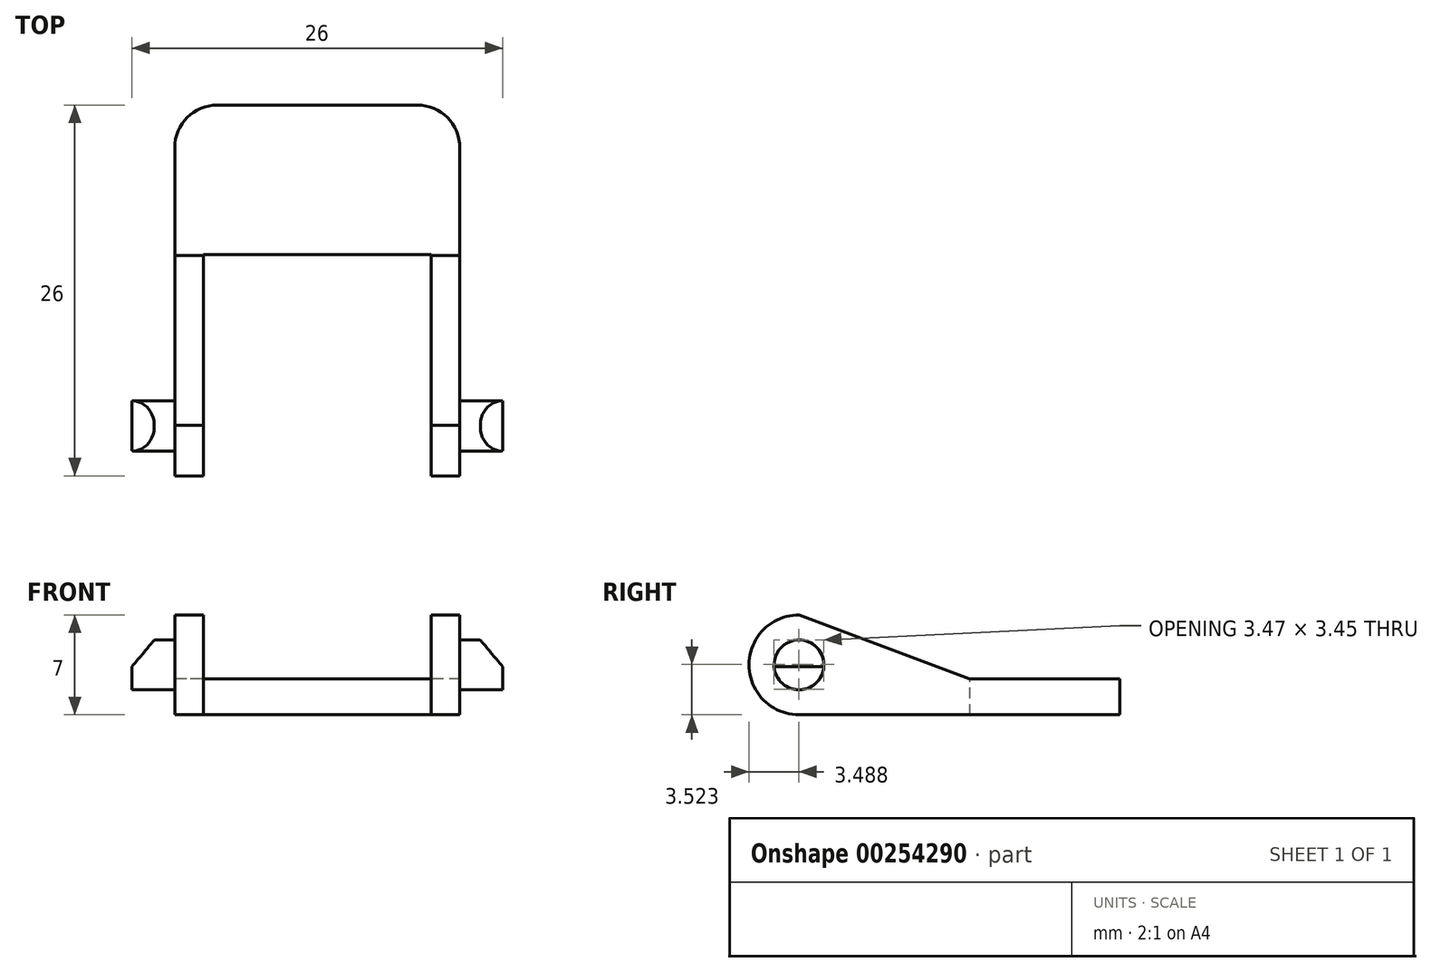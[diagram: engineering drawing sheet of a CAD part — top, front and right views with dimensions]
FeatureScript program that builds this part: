
annotation { "Feature Type Name" : "Feature", "Feature Type Description" : "" }
export const myFeature = defineFeature(function(context is Context, id is Id, definition is map)
    precondition{}
    {
        {
            var Q0;
            Q0=qCreatedBy(makeId("Right.planeOp"),FACE);
            var sketch = newSketch(context, id + "F0", { "sketchPlane" : qUnion([Q0])});
            skLineSegment(sketch, "E0.bottom", {"start": v(-11.1, -3.83) * mm, "end": v(14.9, -3.83) * mm});
            skLineSegment(sketch, "E0.top", {"start": v(-11.1, -6.33) * mm, "end": v(14.9, -6.33) * mm});
            skLineSegment(sketch, "E0.left", {"start": v(-11.1, -3.83) * mm, "end": v(-11.1, -6.33) * mm});
            skLineSegment(sketch, "E0.right", {"start": v(14.9, -3.83) * mm, "end": v(14.9, -6.33) * mm});
            skLineSegment(sketch, "E1", {"start": v(-7.6, -2.83) * mm, "end": v(-7.6, -6.33) * mm});
            skLineSegment(sketch, "E2", {"start": v(-12.06, -7.72) * mm, "end": v(-1, -7.72) * mm});
            skLineSegment(sketch, "E3", {"start": v(-3.27, -2.83) * mm, "end": v(-11.26, -2.83) * mm});
            skPoint(sketch, "E4.orphan", {"position": v(-7.6, -3.83) * mm});
            skCircle(sketch, "E5", {"center": v(-7.6, -2.83) * mm, "radius": 3.5 * mm});
            skLineSegment(sketch, "E6", {"start": v(-7.57, 0.67) * mm, "end": v(4.35, -3.83) * mm});
            skSolve(sketch);
        }
        {
            var Q0;
            {var subQ3=sQuery(id+"F0.wireOp",EDGE,"E3");var subQ7=makeQuery(id+"F0.imprint","INTERSECT",VERTEX,{"derivedFrom":[sQuery(id+"F0.wireOp",EDGE,"E1"),subQ3]});Q0=makeQuery(id+"F0.imprint","IMPRINT",FACE,{"disambiguationData":[TD([[makeQuery(id+"F0.imprint","IMPRINT",EDGE,{"disambiguationData":[TD([[subQ7,-1.0]])],"derivedFrom":subQ3}),-1.0]])]});}
            var Q1;
            {var subQ0=sQuery(id+"F0.wireOp",EDGE,"E5");var subQ1=sQuery(id+"F0.wireOp",EDGE,"E0.bottom");var subQ2=makeQuery(id+"F0.imprint","INTERSECT",VERTEX,{"disambiguationData":[OD(0.0)],"derivedFrom":[subQ1,subQ0]});Q1=makeQuery(id+"F0.imprint","IMPRINT",FACE,{"disambiguationData":[TD([[makeQuery(id+"F0.imprint","IMPRINT",EDGE,{"disambiguationData":[TD([[subQ2,-1.0]])],"derivedFrom":subQ1}),1.0]])]});}
            var Q2;
            {var subQ0=sQuery(id+"F0.wireOp",EDGE,"E1");var subQ1=sQuery(id+"F0.wireOp",EDGE,"E0.bottom");var subQ2=makeQuery(id+"F0.imprint","INTERSECT",VERTEX,{"derivedFrom":[subQ1,subQ0]});Q2=makeQuery(id+"F0.imprint","IMPRINT",FACE,{"disambiguationData":[TD([[makeQuery(id+"F0.imprint","IMPRINT",EDGE,{"disambiguationData":[TD([[subQ2,-1.0]])],"derivedFrom":subQ1}),1.0]])]});}
            var Q3;
            {var subQ0=sQuery(id+"F0.wireOp",EDGE,"E5");var subQ1=sQuery(id+"F0.wireOp",EDGE,"E0.bottom");var subQ2=makeQuery(id+"F0.imprint","INTERSECT",VERTEX,{"disambiguationData":[OD(0.0)],"derivedFrom":[subQ1,subQ0]});Q3=makeQuery(id+"F0.imprint","IMPRINT",FACE,{"disambiguationData":[TD([[makeQuery(id+"F0.imprint","IMPRINT",EDGE,{"disambiguationData":[TD([[subQ2,-1.0]])],"derivedFrom":subQ1}),-1.0]])]});}
            var Q4;
            {var subQ0=sQuery(id+"F0.wireOp",EDGE,"E1");var subQ1=sQuery(id+"F0.wireOp",EDGE,"E0.bottom");var subQ2=makeQuery(id+"F0.imprint","INTERSECT",VERTEX,{"derivedFrom":[subQ1,subQ0]});Q4=makeQuery(id+"F0.imprint","IMPRINT",FACE,{"disambiguationData":[TD([[makeQuery(id+"F0.imprint","IMPRINT",EDGE,{"disambiguationData":[TD([[subQ2,-1.0]])],"derivedFrom":subQ1}),-1.0]])]});}
            var Q5;
            {var subQ0=sQuery(id+"F0.wireOp",EDGE,"E0.right");Q5=makeQuery(id+"F0.imprint","IMPRINT",FACE,{"disambiguationData":[TD([[makeQuery(id+"F0.imprint","IMPRINT",EDGE,{"derivedFrom":subQ0}),-1.0]])]});}
            var Q6;
            {var subQ0=sQuery(id+"F0.wireOp",EDGE,"E6");var subQ1=sQuery(id+"F0.wireOp",EDGE,"E0.bottom");var subQ2=makeQuery(id+"F0.imprint","INTERSECT",VERTEX,{"derivedFrom":[subQ1,subQ0]});Q6=makeQuery(id+"F0.imprint","IMPRINT",FACE,{"disambiguationData":[TD([[makeQuery(id+"F0.imprint","IMPRINT",EDGE,{"disambiguationData":[TD([[subQ2,1.0]])],"derivedFrom":subQ1}),1.0]])]});}
            extrude(context, id + "F1", {"entities" : qUnion([Q0, Q1, Q2, Q3, Q4, Q5, Q6]), "depth" : 20 * mm, "offsetDistance" : 25 * mm});
        }
        {
            var Q0;
            Q0=makeQuery(id+"F1.opExtrude","CAP_FACE",FACE,{"disambiguationData":[OSD([sQuery(id+"F0.wireOp",EDGE,"E0.bottom"),sQuery(id+"F0.wireOp",EDGE,"E0.top"),sQuery(id+"F0.wireOp",EDGE,"E0.right"),sQuery(id+"F0.wireOp",EDGE,"3UJ72o9u-lkwT-MEXm-7RU8-uCdX7h8jatq6"),sQuery(id+"F0.wireOp",EDGE,"Khwpuy8n-Om3G-zq5W-1qji-hnqGbYGo0ahG")])],"isStart":true});
            var sketch = newSketch(context, id + "F2", { "sketchPlane" : qUnion([Q0])});
            skCircle(sketch, "E7", {"center": v(7.6, -2.83) * mm, "radius": 1.75 * mm});
            skSolve(sketch);
        }
        {
            var Q0;
            Q0=makeQuery(id+"F2.imprint","IMPRINT",FACE,{"disambiguationData":[TD([[makeQuery(id+"F2.imprint","IMPRINT",EDGE,{"derivedFrom":sQuery(id+"F2.wireOp",EDGE,"E7")}),1.0]])]});
            extrude(context, id + "F3", {"entities" : qUnion([Q0]), "depth" : 3 * mm, "offsetDistance" : 25 * mm});
        }
        {
            var Q0;
            Q0=qCreatedBy(makeId("Right.planeOp"),FACE);
            cPlane(context, id + "F4", {"entities" : qUnion([Q0]), "cplaneType" : CPlaneType.OFFSET, "offset" : 10 * mm, "width" : 150 * mm, "height" : 150 * mm});
        }
        {
            var Q0;
            Q0=makeQuery(id+"F3.opExtrude","SWEPT_BODY",BODY,{"disambiguationData":[OSD([sQuery(id+"F2.wireOp",EDGE,"E7")])]});
            var Q1;
            Q1=qCreatedBy(id+"F4.planeOp",FACE);
            mirror(context, id + "F5", {"operationType" : NewBodyOperationType.ADD, "entities" : qUnion([Q0]), "mirrorPlane" : qUnion([Q1])});
        }
        {
            var Q0;
            Q0=makeQuery(id+"F1.opExtrude","SWEPT_FACE",FACE,{"disambiguationData":[OSD([sQuery(id+"F0.wireOp",EDGE,"E0.bottom")])]});
            var sketch = newSketch(context, id + "F6", { "sketchPlane" : qUnion([Q0])});
            skLineSegment(sketch, "E8.bottom", {"start": v(18, -30.9) * mm, "end": v(2, -30.9) * mm});
            skLineSegment(sketch, "E8.top", {"start": v(18, 4.4) * mm, "end": v(2, 4.4) * mm});
            skLineSegment(sketch, "E8.left", {"start": v(18, -30.9) * mm, "end": v(18, 4.4) * mm});
            skLineSegment(sketch, "E8.right", {"start": v(2, -30.9) * mm, "end": v(2, 4.4) * mm});
            skSolve(sketch);
        }
        {
            var Q0;
            Q0 = qSketchRegion(id + "F6", true);
            extrude(context, id + "F7", {"entities" : qUnion([Q0]), "operationType" : NewBodyOperationType.REMOVE, "oppositeDirection" : true, "depth" : 25 * mm, "offsetDistance" : 25 * mm, "symmetric" : true});
        }
        {
            var Q0;
            Q0=makeQuery(id+"F1.opExtrude","CAP_EDGE",EDGE,{"disambiguationData":[OSD([sQuery(id+"F0.wireOp",EDGE,"E0.right")])],"isStart":false});
            var Q1;
            Q1=makeQuery(id+"F1.opExtrude","CAP_EDGE",EDGE,{"disambiguationData":[OSD([sQuery(id+"F0.wireOp",EDGE,"E0.right")])],"isStart":true});
            fillet(context, id + "F8", {"entities" : qUnion([Q0, Q1]), "tangentPropagation" : true, "radius" : 3 * mm, "defaultsChanged" : true, "vertexSettings" : [], "allowEdgeOverflow" : false});
        }
        {
            var Q0;
            Q0=qCreatedBy(makeId("Front.planeOp"),FACE);
            var sketch = newSketch(context, id + "F9", { "sketchPlane" : qUnion([Q0])});
            skLineSegment(sketch, "E9", {"start": v(20.35, 0.2) * mm, "end": v(23.9, -4.05) * mm});
            skLineSegment(sketch, "E10", {"start": v(23.9, -4.05) * mm, "end": v(23.9, 7.16) * mm});
            skLineSegment(sketch, "E11.MirrorCS", {"start": v(-3.9, -4.05) * mm, "end": v(-3.9, 7.16) * mm});
            skLineSegment(sketch, "E12.MirrorCS", {"start": v(-0.35, 0.2) * mm, "end": v(-3.9, -4.05) * mm});
            skLineSegment(sketch, "E13", {"start": v(20.35, 0.2) * mm, "end": v(20.35, 3.3) * mm});
            skLineSegment(sketch, "E14", {"start": v(20.35, 3.3) * mm, "end": v(-0.35, 3.3) * mm});
            skLineSegment(sketch, "E15", {"start": v(-0.35, 0.2) * mm, "end": v(-0.35, 3.3) * mm});
            skLineSegment(sketch, "E16", {"start": v(23.9, 7.16) * mm, "end": v(-3.9, 7.16) * mm});
            skSolve(sketch);
        }
        {
            var Q0;
            Q0 = qSketchRegion(id + "F9", true);
            extrude(context, id + "F10", {"entities" : qUnion([Q0]), "depth" : 25 * mm, "offsetDistance" : 25 * mm});
        }
        {
            var Q0;
            Q0=makeQuery(id+"F10.opExtrude","SWEPT_BODY",BODY,{"disambiguationData":[OSD([sQuery(id+"F9.wireOp",EDGE,"E9"),sQuery(id+"F9.wireOp",EDGE,"E10"),sQuery(id+"F9.wireOp",EDGE,"E11.MirrorCS"),sQuery(id+"F9.wireOp",EDGE,"E12.MirrorCS"),sQuery(id+"F9.wireOp",EDGE,"E13"),sQuery(id+"F9.wireOp",EDGE,"E14"),sQuery(id+"F9.wireOp",EDGE,"E15"),sQuery(id+"F9.wireOp",EDGE,"E16")])]});
            var Q1;
            Q1=makeQuery(id+"F1.opExtrude","SWEPT_BODY",BODY,{"disambiguationData":[OSD([sQuery(id+"F0.wireOp",EDGE,"E0.bottom"),sQuery(id+"F0.wireOp",EDGE,"E0.top"),sQuery(id+"F0.wireOp",EDGE,"E0.right"),sQuery(id+"F0.wireOp",EDGE,"E5"),sQuery(id+"F0.wireOp",EDGE,"E6")])]});
            booleanBodies(context, id + "F11", {"operationType" : BooleanOperationType.SUBTRACTION, "tools" : qUnion([Q0]), "targets" : qUnion([Q1])});
        }
    });
